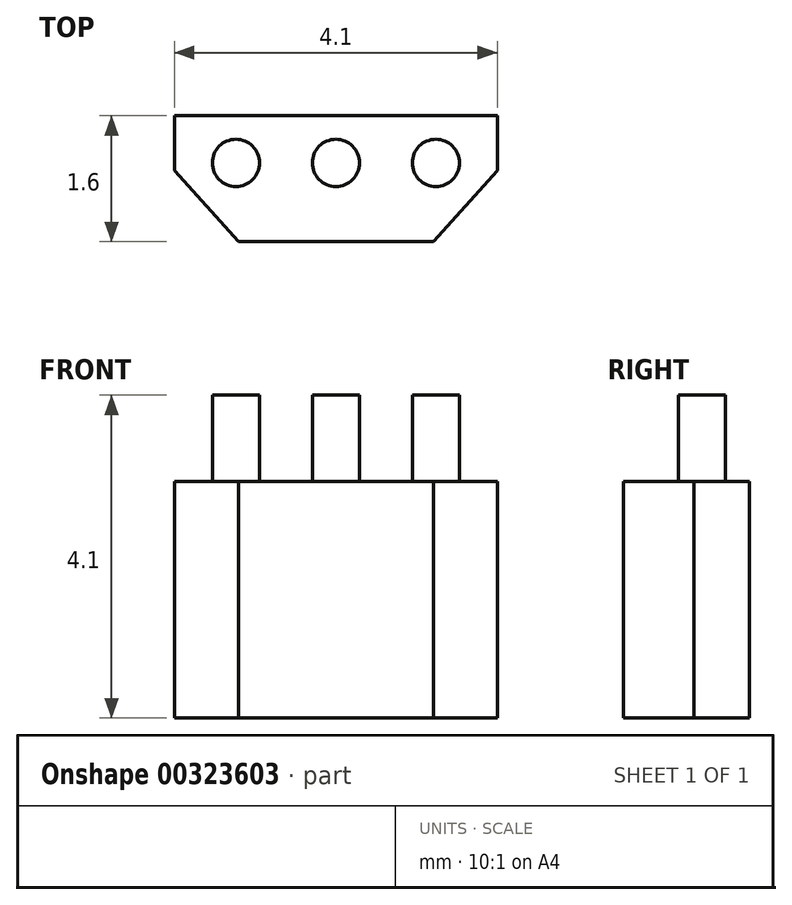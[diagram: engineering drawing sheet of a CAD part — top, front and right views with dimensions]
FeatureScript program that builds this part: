
annotation { "Feature Type Name" : "Feature", "Feature Type Description" : "" }
export const myFeature = defineFeature(function(context is Context, id is Id, definition is map)
    precondition{}
    {
        {
            var Q0;
            Q0=qCreatedBy(makeId("Top.planeOp"),FACE);
            var sketch = newSketch(context, id + "F0", { "sketchPlane" : qUnion([Q0])});
            skCircle(sketch, "E0", {"center": v(0, 0) * mm, "radius": 0.3 * mm});
            skCircle(sketch, "E1", {"center": v(1.27, 0) * mm, "radius": 0.3 * mm});
            skCircle(sketch, "E2", {"center": v(-1.27, 0) * mm, "radius": 0.3 * mm});
            skSolve(sketch);
        }
        {
            var Q0;
            Q0 = qSketchRegion(id + "F0", true);
            extrude(context, id + "F1", {"entities" : qUnion([Q0]), "offsetDistance" : 25 * mm, "depth" : 1.1 * mm});
        }
        {
            var Q0;
            Q0=makeQuery(id+"F1.opExtrude","CAP_FACE",FACE,{"disambiguationData":[OSD([sQuery(id+"F0.wireOp",EDGE,"E0")])],"isStart":true});
            var sketch = newSketch(context, id + "F2", { "sketchPlane" : qUnion([Q0])});
            skLineSegment(sketch, "E3", {"start": v(-1.24, 1) * mm, "end": v(1.24, 1) * mm});
            skLineSegment(sketch, "E4", {"start": v(-1.24, 1) * mm, "end": v(-2.05, 0.1) * mm});
            skLineSegment(sketch, "E5", {"start": v(-2.05, 0.1) * mm, "end": v(-2.05, -0.6) * mm});
            skLineSegment(sketch, "E6", {"start": v(-2.05, -0.6) * mm, "end": v(2.05, -0.6) * mm});
            skLineSegment(sketch, "E7", {"start": v(2.05, -0.6) * mm, "end": v(2.05, 0.1) * mm});
            skLineSegment(sketch, "E8", {"start": v(2.05, 0.1) * mm, "end": v(1.24, 1) * mm});
            skSolve(sketch);
        }
        {
            var Q0;
            Q0 = qSketchRegion(id + "F2", true);
            extrude(context, id + "F3", {"entities" : qUnion([Q0]), "operationType" : NewBodyOperationType.ADD, "offsetDistance" : 25 * mm, "depth" : 3 * mm});
        }
    });
